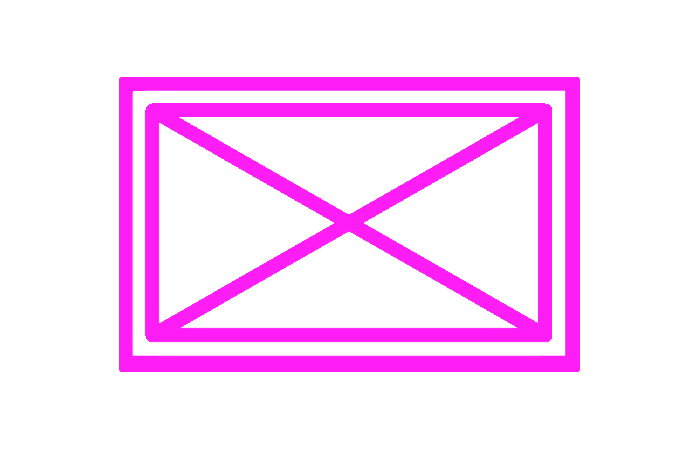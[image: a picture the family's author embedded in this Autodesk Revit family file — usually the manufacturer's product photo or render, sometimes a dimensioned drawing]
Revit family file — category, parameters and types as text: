
# Revit family: Контроллер AGRG R2 RACK_на грани
name_source: partatom
category: Электрооборудование
units: mm (PartAtom-declared; Revit-internal decimal feet)

## family parameters
Общий = Нет
Основа = Грань
При загрузке вырезать с полостями = Нет
Размер круглого соединителя = Использовать диаметр
Тип детали = Другая панель
Точка расчета площади = Нет

## types (1)
- Контроллер AGRG R2 RACK
    ADSK_Единица измерения = шт.
    ADSK_Завод-изготовитель = ООО «Агрегатор»
    ADSK_Код изделия = CCTLR2R
    ADSK_Количество = 1
    ADSK_Коэффициент мощности = 1
    ADSK_Марка = AGRG ЦОД
    ADSK_Масса = 2.7
    ADSK_Наименование = Специализированный контроллер AGRG R2 Rack для IT-инфраструктуры (защита телеком. шкафов). Габариты: 410 х 190 х 43 мм (без кронштейнов), исполнение 1U. Подключение до 2-х специализированных ручек со встроенными считывателями. Оснащен АКБ (до 3-х часов автономн. работы). Работает под управлением ПО SIGUR.
    ADSK_Наименование краткое = Контроллер
    ADSK_Обозначение = ARD
    ITV_LCS_Высота U = 1
    ITV_SUB_УГО на структурной схеме = УГО_Контроллер
    URL = https://skud.agrg.ru
    Группа модели = Оборудование
    Изображение типоразмера = ARD.png
    Описание = ITV
    Отметка по умолчанию = 1219 мм
